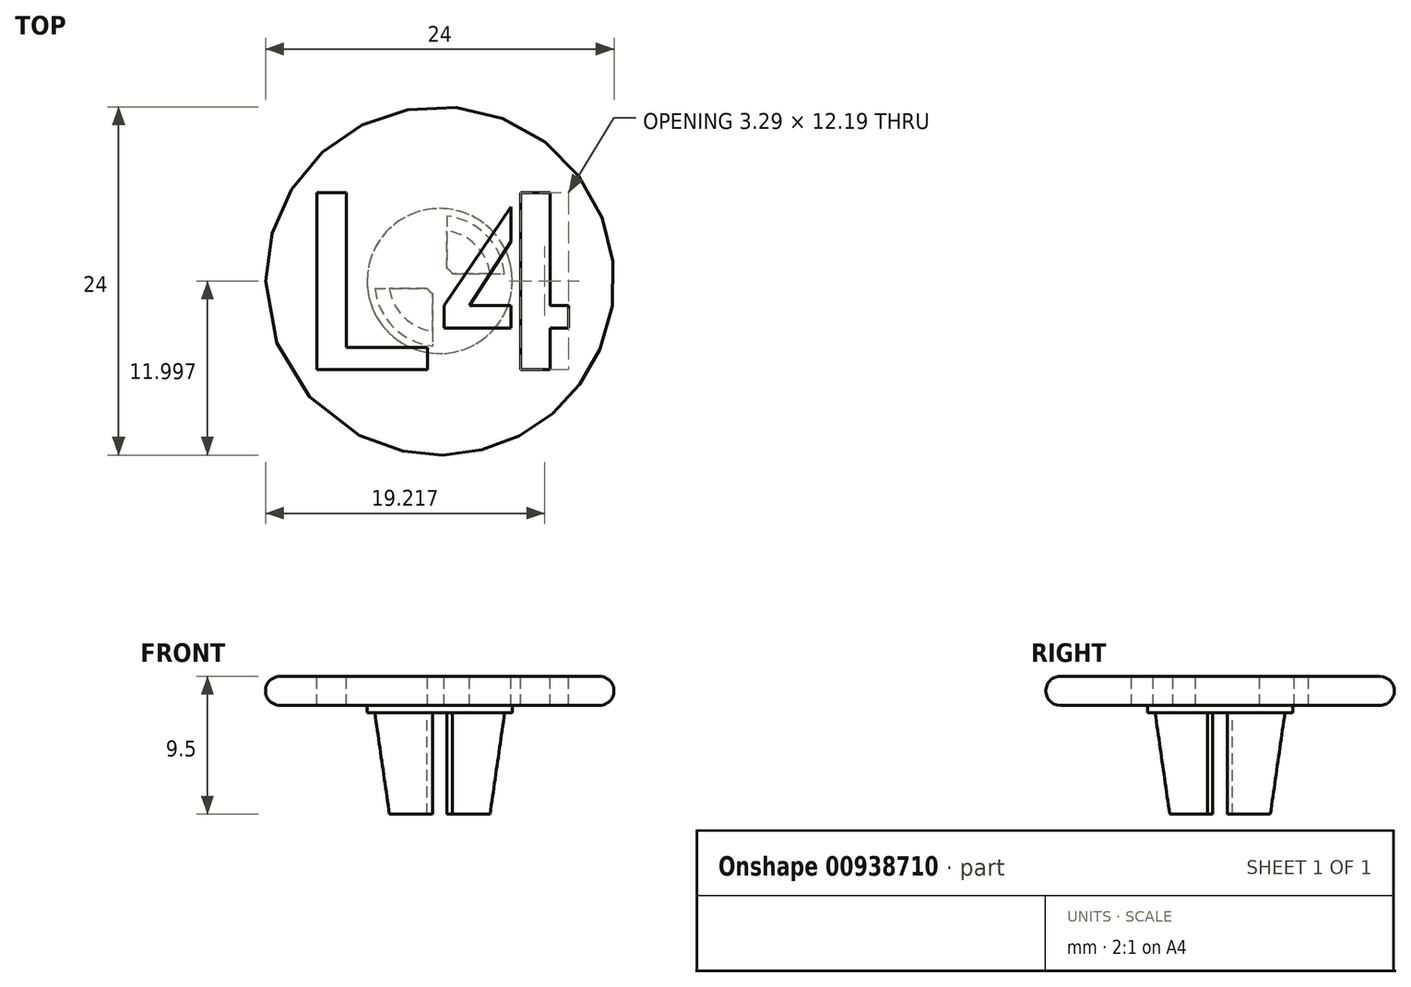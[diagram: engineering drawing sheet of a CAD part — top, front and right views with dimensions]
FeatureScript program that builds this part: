
annotation { "Feature Type Name" : "Feature", "Feature Type Description" : "" }
export const myFeature = defineFeature(function(context is Context, id is Id, definition is map)
    precondition{}
    {
        {
            var Q0;
            Q0=qCreatedBy(makeId("Front.planeOp"),FACE);
            var sketch = newSketch(context, id + "F0", { "sketchPlane" : qUnion([Q0])});
            skLineSegment(sketch, "E0.bottom", {"start": v(0, 0) * mm, "end": v(-5, 0) * mm});
            skLineSegment(sketch, "E0.top", {"start": v(0, 0.5) * mm, "end": v(-5, 0.5) * mm});
            skLineSegment(sketch, "E0.left", {"start": v(0, 0) * mm, "end": v(0, 0.5) * mm});
            skLineSegment(sketch, "E0.right", {"start": v(-5, 0) * mm, "end": v(-5, 0.5) * mm});
            skLineSegment(sketch, "E1.bottom", {"start": v(0, 0.5) * mm, "end": v(-11, 0.5) * mm});
            skLineSegment(sketch, "E1.top", {"start": v(0, 2.5) * mm, "end": v(-11, 2.5) * mm});
            skLineSegment(sketch, "E1.left", {"start": v(0, 0.5) * mm, "end": v(0, 2.5) * mm});
            skArc(sketch, "E2", {"start": v(-11, 2.5) * mm, "mid": v(-12, 1.5) * mm, "end": v(-11, 0.5) * mm});
            skPoint(sketch, "E3", {"position": v(0, 1.5) * mm});
            skSolve(sketch);
        }
        {
            var Q0;
            Q0 = qSketchRegion(id + "F0", true);
            var Q1;
            Q1=sQuery(id+"F0.wireOp",EDGE,"E1.left");
            revolve(context, id + "F1", {"surfaceOperationType" : NewSurfaceOperationType.NEW, "entities" : qUnion([Q0]), "axis" : qUnion([Q1]), "revolveType" : RevolveType.FULL});
        }
        {
            var Q0;
            Q0=qCreatedBy(makeId("Front.planeOp"),FACE);
            var sketch = newSketch(context, id + "F2", { "sketchPlane" : qUnion([Q0])});
            skLineSegment(sketch, "E4", {"start": v(1, 0) * mm, "end": v(1, -7) * mm});
            skLineSegment(sketch, "E5", {"start": v(1, -7) * mm, "end": v(3.5, -7) * mm});
            skLineSegment(sketch, "E6", {"start": v(3.5, -7) * mm, "end": v(4.5, 0) * mm});
            skLineSegment(sketch, "E7", {"start": v(4.5, 0) * mm, "end": v(1, 0) * mm});
            skLineSegment(sketch, "E8", {"start": v(0, 0) * mm, "end": v(0, -2.56) * mm});
            skSolve(sketch);
        }
        {
            var Q0;
            Q0 = qSketchRegion(id + "F2", true);
            var Q1;
            Q1=sQuery(id+"F2.wireOp",EDGE,"E8");
            revolve(context, id + "F3", {"operationType" : NewBodyOperationType.ADD, "surfaceOperationType" : NewSurfaceOperationType.NEW, "entities" : qUnion([Q0]), "axis" : qUnion([Q1]), "revolveType" : RevolveType.FULL});
        }
        {
            var Q0;
            Q0=makeQuery(id+"F3.opRevolve","SWEPT_FACE",FACE,{"disambiguationData":[OSD([sQuery(id+"F2.wireOp",EDGE,"E5")])]});
            var sketch = newSketch(context, id + "F4", { "sketchPlane" : qUnion([Q0])});
            skLineSegment(sketch, "E9.bottom", {"start": v(10, 0.5) * mm, "end": v(-10, 0.5) * mm});
            skLineSegment(sketch, "E9.top", {"start": v(10, -0.5) * mm, "end": v(-10, -0.5) * mm});
            skLineSegment(sketch, "E9.left", {"start": v(10, 0.5) * mm, "end": v(10, -0.5) * mm});
            skLineSegment(sketch, "E9.right", {"start": v(-10, 0.5) * mm, "end": v(-10, -0.5) * mm});
            skPoint(sketch, "E9.middle", {"position": v(0, 0) * mm});
            skLineSegment(sketch, "E10.bottom", {"start": v(-0.5, 10) * mm, "end": v(0.5, 10) * mm});
            skLineSegment(sketch, "E10.top", {"start": v(-0.5, -10) * mm, "end": v(0.5, -10) * mm});
            skLineSegment(sketch, "E10.left", {"start": v(-0.5, 10) * mm, "end": v(-0.5, -10) * mm});
            skLineSegment(sketch, "E10.right", {"start": v(0.5, 10) * mm, "end": v(0.5, -10) * mm});
            skLineSegment(sketch, "E11.bottom", {"start": v(0.5, 0.5) * mm, "end": v(6.43, 0.5) * mm});
            skLineSegment(sketch, "E11.top", {"start": v(0.5, 5.8) * mm, "end": v(6.43, 5.8) * mm});
            skLineSegment(sketch, "E11.left", {"start": v(0.5, 0.5) * mm, "end": v(0.5, 5.8) * mm});
            skLineSegment(sketch, "E11.right", {"start": v(6.43, 0.5) * mm, "end": v(6.43, 5.8) * mm});
            skLineSegment(sketch, "E12.bottom", {"start": v(-0.5, -0.5) * mm, "end": v(-5.6, -0.5) * mm});
            skLineSegment(sketch, "E12.top", {"start": v(-0.5, -5.9) * mm, "end": v(-5.6, -5.9) * mm});
            skLineSegment(sketch, "E12.left", {"start": v(-0.5, -0.5) * mm, "end": v(-0.5, -5.9) * mm});
            skLineSegment(sketch, "E12.right", {"start": v(-5.6, -0.5) * mm, "end": v(-5.6, -5.9) * mm});
            skSolve(sketch);
        }
        {
            var Q0;
            Q0 = qSketchRegion(id + "F4", true);
            var Q1;
            Q1=makeQuery(id+"F3.boolean.opBoolean","SPLIT",FACE,{"disambiguationData":[TD([makeQuery(id+"F1.opRevolve","SWEPT_FACE",FACE,{"disambiguationData":[OSD([sQuery(id+"F0.wireOp",EDGE,"E0.right")])]})])],"derivedFrom":makeQuery(id+"F1.opRevolve","SWEPT_FACE",FACE,{"disambiguationData":[OSD([sQuery(id+"F0.wireOp",EDGE,"E0.bottom")])]})});
            extrude(context, id + "F5", {"entities" : qUnion([Q0]), "operationType" : NewBodyOperationType.REMOVE, "endBound" : BoundingType.UP_TO_SURFACE, "oppositeDirection" : true, "depth" : 25 * mm, "endBoundEntityFace" : qUnion([Q1]), "offsetDistance" : 25 * mm});
        }
        {
            var Q0;
            Q0=makeQuery(id+"F1.opRevolve","SWEPT_FACE",FACE,{"disambiguationData":[OSD([sQuery(id+"F0.wireOp",EDGE,"E1.top")])]});
            var sketch = newSketch(context, id + "F6", { "sketchPlane" : qUnion([Q0])});
            skText(sketch, "E13", { "text": "L4", "fontName": "AllertaStencil-Regular.ttf"});
            skPoint(sketch, "E14", {"position": v(0, 0) * mm});
            const initialGuessF6  = {"E13": [-0.01, -0.0061, 1, 0, 0.0122]};
            skSetInitialGuess(sketch, initialGuessF6);
            skSolve(sketch);
        }
        {
            var Q0;
            Q0 = qSketchRegion(id + "F6", true);
            var Q1;
            Q1=makeQuery(id+"F1.opRevolve","SWEPT_FACE",FACE,{"disambiguationData":[OSD([sQuery(id+"F0.wireOp",EDGE,"E1.bottom")])]});
            extrude(context, id + "F7", {"entities" : qUnion([Q0]), "endBound" : BoundingType.UP_TO_SURFACE, "oppositeDirection" : true, "depth" : 25 * mm, "endBoundEntityFace" : qUnion([Q1]), "offsetDistance" : 25 * mm});
        }
        {
            var Q0;
            Q0=makeQuery(id+"F7.opExtrude","SWEPT_BODY",BODY,{"disambiguationData":[OSD([sQuery(id+"F6.wireOp",EDGE,"E13.sketch_text.stroke-0"),sQuery(id+"F6.wireOp",EDGE,"E13.sketch_text.stroke-1"),sQuery(id+"F6.wireOp",EDGE,"E13.sketch_text.stroke-2"),sQuery(id+"F6.wireOp",EDGE,"E13.sketch_text.stroke-3"),sQuery(id+"F6.wireOp",EDGE,"E13.sketch_text.stroke-4"),sQuery(id+"F6.wireOp",EDGE,"E13.sketch_text.stroke-5")])]});
            var Q1;
            Q1=makeQuery(id+"F7.opExtrude","SWEPT_BODY",BODY,{"disambiguationData":[OSD([sQuery(id+"F6.wireOp",EDGE,"E13.sketch_text.stroke-6"),sQuery(id+"F6.wireOp",EDGE,"E13.sketch_text.stroke-7"),sQuery(id+"F6.wireOp",EDGE,"E13.sketch_text.stroke-8"),sQuery(id+"F6.wireOp",EDGE,"E13.sketch_text.stroke-9"),sQuery(id+"F6.wireOp",EDGE,"E13.sketch_text.stroke-10"),sQuery(id+"F6.wireOp",EDGE,"E13.sketch_text.stroke-11"),sQuery(id+"F6.wireOp",EDGE,"E13.sketch_text.stroke-12"),sQuery(id+"F6.wireOp",EDGE,"E13.sketch_text.stroke-13")])]});
            var Q2;
            Q2=makeQuery(id+"F7.opExtrude","SWEPT_BODY",BODY,{"disambiguationData":[OSD([sQuery(id+"F6.wireOp",EDGE,"E13.sketch_text.stroke-14"),sQuery(id+"F6.wireOp",EDGE,"E13.sketch_text.stroke-15"),sQuery(id+"F6.wireOp",EDGE,"E13.sketch_text.stroke-16"),sQuery(id+"F6.wireOp",EDGE,"E13.sketch_text.stroke-17"),sQuery(id+"F6.wireOp",EDGE,"E13.sketch_text.stroke-18"),sQuery(id+"F6.wireOp",EDGE,"E13.sketch_text.stroke-19"),sQuery(id+"F6.wireOp",EDGE,"E13.sketch_text.stroke-20")])]});
            var Q3;
            Q3=makeQuery(id+"F1.opRevolve","SWEPT_BODY",BODY,{"disambiguationData":[OSD([sQuery(id+"F0.wireOp",EDGE,"E0.bottom"),sQuery(id+"F0.wireOp",EDGE,"E0.left"),sQuery(id+"F0.wireOp",EDGE,"E0.right"),sQuery(id+"F0.wireOp",EDGE,"E1.bottom"),sQuery(id+"F0.wireOp",EDGE,"E1.top"),sQuery(id+"F0.wireOp",EDGE,"E1.left"),sQuery(id+"F0.wireOp",EDGE,"E2")])]});
            booleanBodies(context, id + "F8", {"operationType" : BooleanOperationType.SUBTRACTION, "tools" : qUnion([Q0, Q1, Q2]), "targets" : qUnion([Q3]), "keepTools" : true});
        }
    });
